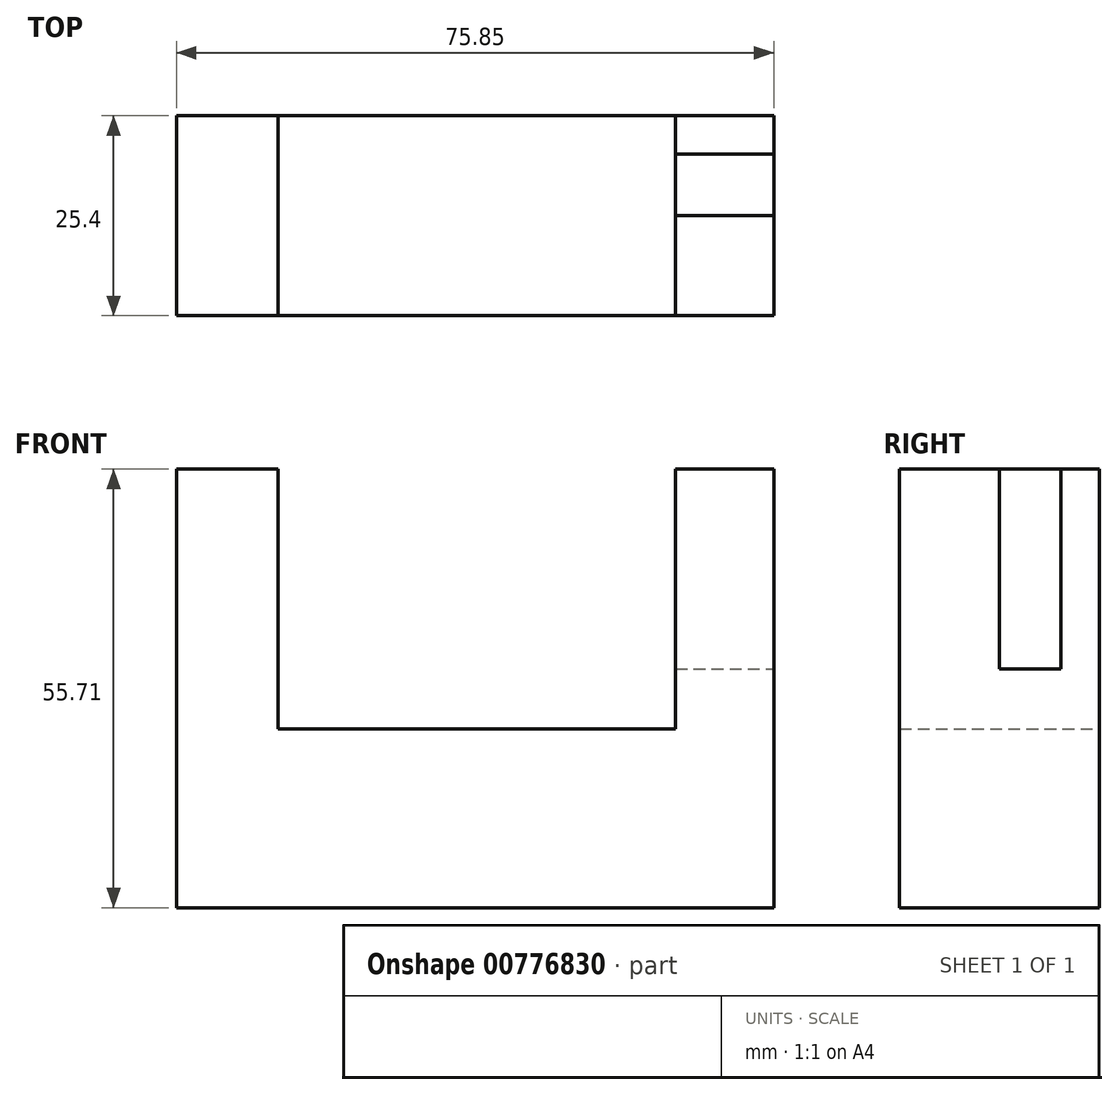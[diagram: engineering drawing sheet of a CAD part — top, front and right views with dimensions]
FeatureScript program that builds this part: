
annotation { "Feature Type Name" : "Feature", "Feature Type Description" : "" }
export const myFeature = defineFeature(function(context is Context, id is Id, definition is map)
    precondition{}
    {
        {
            var Q0;
            Q0=qCreatedBy(makeId("Front.planeOp"),FACE);
            var sketch = newSketch(context, id + "F0", { "sketchPlane" : qUnion([Q0])});
            skLineSegment(sketch, "E0.bottom", {"start": v(0, 0) * mm, "end": v(-75.85, 0) * mm});
            skLineSegment(sketch, "E0.top", {"start": v(0, 55.71) * mm, "end": v(-12.48, 55.71) * mm});
            skLineSegment(sketch, "E0.left", {"start": v(0, 0) * mm, "end": v(0, 55.71) * mm});
            skLineSegment(sketch, "E0.right", {"start": v(-75.85, 0) * mm, "end": v(-75.85, 55.71) * mm});
            skLineSegment(sketch, "E1.top", {"start": v(-62.96, 22.69) * mm, "end": v(-12.48, 22.69) * mm});
            skLineSegment(sketch, "E1.left", {"start": v(-62.96, 55.71) * mm, "end": v(-62.96, 22.69) * mm});
            skLineSegment(sketch, "E1.right", {"start": v(-12.48, 55.71) * mm, "end": v(-12.48, 22.69) * mm});
            skLineSegment(sketch, "E2.trimOffspring", {"start": v(-62.96, 55.71) * mm, "end": v(-75.85, 55.71) * mm});
            skSolve(sketch);
        }
        {
            var Q0;
            Q0=makeQuery(id+"F0.imprint","IMPRINT",FACE,{"disambiguationData":[TD([[makeQuery(id+"F0.imprint","IMPRINT",EDGE,{"derivedFrom":sQuery(id+"F0.wireOp",EDGE,"E0.bottom")}),-1.0]])]});
            extrude(context, id + "F1", {"entities" : qUnion([Q0]), "depth" : 25.4 * mm, "offsetDistance" : 25.4 * mm});
        }
        {
            var Q0;
            Q0=makeQuery(id+"F1.opExtrude","SWEPT_FACE",FACE,{"disambiguationData":[OSD([sQuery(id+"F0.wireOp",EDGE,"E0.top")])]});
            var sketch = newSketch(context, id + "F2", { "sketchPlane" : qUnion([Q0])});
            skLineSegment(sketch, "E3.bottom", {"start": v(-12.48, -4.9) * mm, "end": v(0, -4.9) * mm});
            skLineSegment(sketch, "E3.top", {"start": v(-12.48, -12.7) * mm, "end": v(0, -12.7) * mm});
            skLineSegment(sketch, "E3.left", {"start": v(-12.48, -4.9) * mm, "end": v(-12.48, -12.7) * mm});
            skLineSegment(sketch, "E3.right", {"start": v(0, -4.9) * mm, "end": v(0, -12.7) * mm});
            skSolve(sketch);
        }
        {
            var Q0;
            Q0 = qSketchRegion(id + "F2", true);
            extrude(context, id + "F3", {"entities" : qUnion([Q0]), "operationType" : NewBodyOperationType.REMOVE, "oppositeDirection" : true, "depth" : 25.4 * mm, "offsetDistance" : 25.4 * mm});
        }
    });
